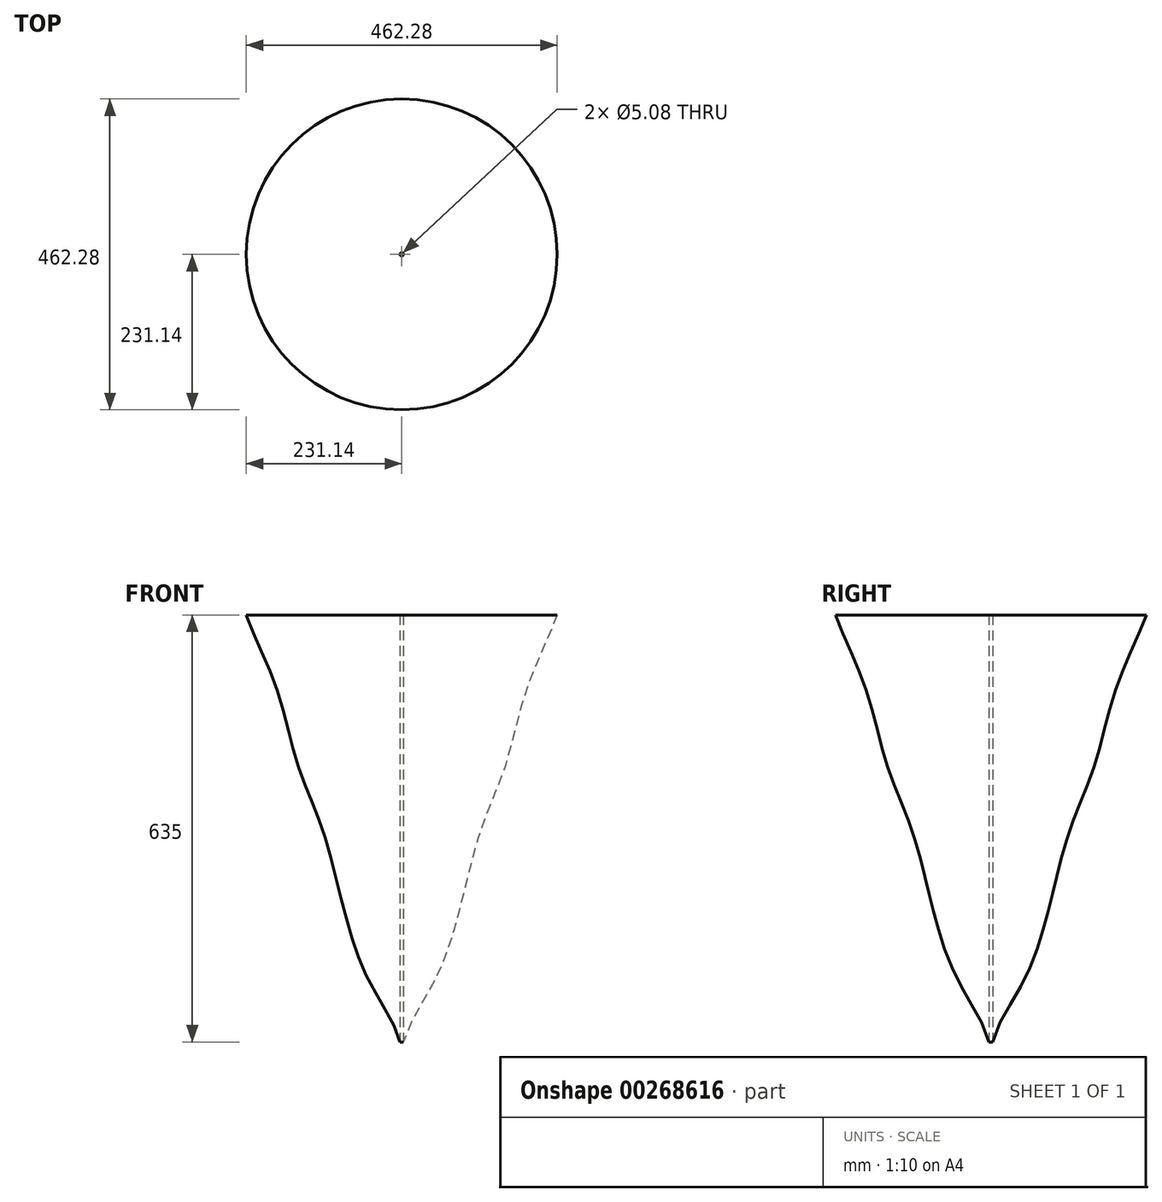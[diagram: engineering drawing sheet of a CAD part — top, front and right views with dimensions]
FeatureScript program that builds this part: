
annotation { "Feature Type Name" : "Feature", "Feature Type Description" : "" }
export const myFeature = defineFeature(function(context is Context, id is Id, definition is map)
    precondition{}
    {
        {
            var Q0;
            Q0=qCreatedBy(makeId("Front.planeOp"),FACE);
            var sketch = newSketch(context, id + "F0", { "sketchPlane" : qUnion([Q0])});
            skLineSegment(sketch, "E0", {"start": v(0, 0) * mm, "end": v(2.54, 0) * mm});
            skLineSegment(sketch, "E1", {"start": v(0, 0) * mm, "end": v(-2.54, 0) * mm});
            skLineSegment(sketch, "E2", {"start": v(2.54, 0) * mm, "end": v(2.54, 635) * mm});
            skLineSegment(sketch, "E3", {"start": v(-2.54, 0) * mm, "end": v(-2.54, 635) * mm});
            skLineSegment(sketch, "E4", {"start": v(-2.54, 635) * mm, "end": v(-231.14, 635) * mm});
            skLineSegment(sketch, "E5", {"start": v(2.54, 635) * mm, "end": v(231.14, 635) * mm});
            skLineSegment(sketch, "E6", {"start": v(0, 0) * mm, "end": v(0, 670.23) * mm});
            skFitSpline(sketch, "E7", {"points": [v(2.54, 0) * mm, v(47.54, 88.42) * mm, v(86.21, 198.24) * mm, v(118.7, 318.89) * mm, v(154.27, 411.7) * mm, v(185.2, 523.06) * mm, v(231.14, 635) * mm], "startDerivative": vector(144.55, 570.7) * mm, "endDerivative": vector(224.33, 599.12) * mm});
            skFitSpline(sketch, "E8.MirrorCS", {"points": [v(-2.54, 0) * mm, v(-47.54, 88.42) * mm, v(-86.21, 198.24) * mm, v(-118.7, 318.89) * mm, v(-154.27, 411.7) * mm, v(-185.2, 523.06) * mm, v(-231.14, 635) * mm], "startDerivative": vector(-144.55, 570.7) * mm, "endDerivative": vector(-224.33, 599.12) * mm});
            skSolve(sketch);
        }
        {
            var Q0;
            Q0=makeQuery(id+"F0.imprint","IMPRINT",FACE,{"disambiguationData":[TD([[makeQuery(id+"F0.imprint","IMPRINT",EDGE,{"derivedFrom":sQuery(id+"F0.wireOp",EDGE,"E3")}),1.0]])]});
            var Q1;
            Q1=makeQuery(id+"F0.imprint","IMPRINT",FACE,{"disambiguationData":[TD([[makeQuery(id+"F0.imprint","IMPRINT",EDGE,{"derivedFrom":sQuery(id+"F0.wireOp",EDGE,"E2")}),-1.0]])]});
            var Q2;
            Q2=sQuery(id+"F0.wireOp",EDGE,"E6");
            revolve(context, id + "F1", {"entities" : qUnion([Q0, Q1]), "axis" : qUnion([Q2]), "revolveType" : RevolveType.FULL});
        }
    });
